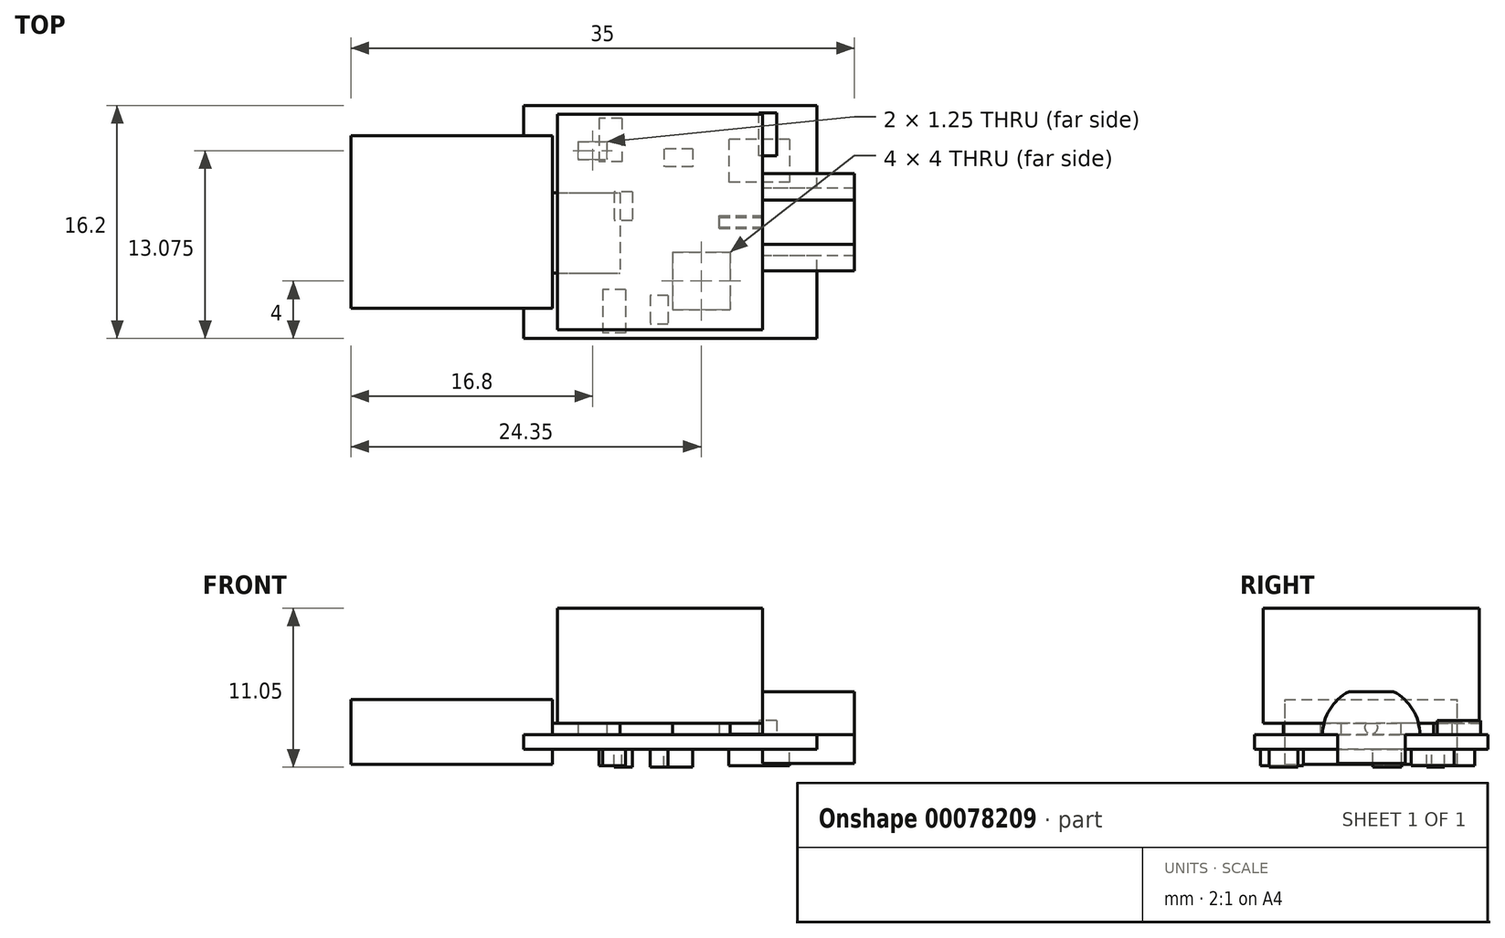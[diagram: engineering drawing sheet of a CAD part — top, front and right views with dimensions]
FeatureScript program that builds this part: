
annotation { "Feature Type Name" : "Feature", "Feature Type Description" : "" }
export const myFeature = defineFeature(function(context is Context, id is Id, definition is map)
    precondition{}
    {
        {
            var Q0;
            Q0=qCreatedBy(makeId("Top.planeOp"),FACE);
            var sketch = newSketch(context, id + "F0", { "sketchPlane" : qUnion([Q0])});
            skLineSegment(sketch, "E0.bottom", {"start": v(10.2, -8.1) * mm, "end": v(-10.2, -8.1) * mm});
            skLineSegment(sketch, "E0.top", {"start": v(10.2, 8.1) * mm, "end": v(-10.2, 8.1) * mm});
            skLineSegment(sketch, "E0.left", {"start": v(10.2, -8.1) * mm, "end": v(10.2, 8.1) * mm});
            skLineSegment(sketch, "E0.right", {"start": v(-10.2, -8.1) * mm, "end": v(-10.2, 8.1) * mm});
            skPoint(sketch, "E0.middle", {"position": v(0, 0) * mm});
            skSolve(sketch);
        }
        {
            var Q0;
            Q0=makeQuery(id+"F0.imprint","IMPRINT",FACE,{"disambiguationData":[TD([[makeQuery(id+"F0.imprint","IMPRINT",EDGE,{"derivedFrom":sQuery(id+"F0.wireOp",EDGE,"E0.bottom")}),-1.0]])]});
            extrude(context, id + "F1", {"entities" : qUnion([Q0]), "oppositeDirection" : true, "depth" : 1 * mm});
        }
        {
            var Q0;
            Q0=makeQuery(id+"F1.opExtrude","SWEPT_FACE",FACE,{"disambiguationData":[OSD([sQuery(id+"F0.wireOp",EDGE,"E0.right")])]});
            var sketch = newSketch(context, id + "F2", { "sketchPlane" : qUnion([Q0])});
            skLineSegment(sketch, "E1.bottom", {"start": v(6, -2.05) * mm, "end": v(-6, -2.05) * mm});
            skLineSegment(sketch, "E1.top", {"start": v(6, 2.45) * mm, "end": v(-6, 2.45) * mm});
            skLineSegment(sketch, "E1.left", {"start": v(6, -2.05) * mm, "end": v(6, 2.45) * mm});
            skLineSegment(sketch, "E1.right", {"start": v(-6, -2.05) * mm, "end": v(-6, 2.45) * mm});
            skPoint(sketch, "E1.middle", {"position": v(0, 0.2) * mm});
            skSolve(sketch);
        }
        {
            var Q0;
            Q0=qSketchRegion(id+"F2",true);
            extrude(context, id + "F3", {"entities" : qUnion([Q0]), "operationType" : NewBodyOperationType.ADD, "depth" : 12 * mm, "hasSecondDirection" : true, "secondDirectionOppositeDirection" : true, "secondDirectionDepth" : 2 * mm});
        }
        {
            var Q0;
            Q0=makeQuery(id+"F1.opExtrude","SWEPT_FACE",FACE,{"disambiguationData":[OSD([sQuery(id+"F0.wireOp",EDGE,"E0.left")])]});
            var sketch = newSketch(context, id + "F4", { "sketchPlane" : qUnion([Q0])});
            skLineSegment(sketch, "E2.top", {"start": v(-2.35, -2) * mm, "end": v(2.35, -2) * mm});
            skLineSegment(sketch, "E2.left", {"start": v(-2.35, 0) * mm, "end": v(-2.35, -2) * mm});
            skLineSegment(sketch, "E2.right", {"start": v(2.35, 0) * mm, "end": v(2.35, -2) * mm});
            skLineSegment(sketch, "E3", {"start": v(0, 0) * mm, "end": v(0, 1.3) * mm, "construction": true});
            skPoint(sketch, "E3.endSnap0", {"position": v(0, 0) * mm});
            skLineSegment(sketch, "E4", {"start": v(-2.35, 0) * mm, "end": v(-3.37, 0) * mm});
            skLineSegment(sketch, "E5", {"start": v(2.35, 0) * mm, "end": v(3.38, 0) * mm});
            skArc(sketch, "E6", {"start": v(3.38, 0) * mm, "mid": v(2.88, 1.76) * mm, "end": v(1.55, 3) * mm});
            skLineSegment(sketch, "E7", {"start": v(-1.55, 3) * mm, "end": v(1.55, 3) * mm});
            skArc(sketch, "E8.trimOffspring", {"start": v(-1.55, 3) * mm, "mid": v(-2.88, 1.76) * mm, "end": v(-3.37, 0) * mm});
            skSolve(sketch);
        }
        {
            var Q0;
            {var subQ0=sQuery(id+"F4.wireOp",EDGE,"E2.top");Q0=makeQuery(id+"F4.imprint","IMPRINT",FACE,{"disambiguationData":[TD([[makeQuery(id+"F4.imprint","IMPRINT",EDGE,{"derivedFrom":subQ0}),1.0]])]});}
            var Q1;
            {var subQ0=sQuery(id+"F4.wireOp",EDGE,"E2.left");var subQ1=sQuery(id+"F0.wireOp",EDGE,"E0.left");var subQ4=makeQuery(id+"F1.opExtrude","CAP_EDGE",EDGE,{"disambiguationData":[OSD([subQ1])],"isStart":false});var subQ5=makeQuery(id+"F4.imprint","INTERSECT",VERTEX,{"derivedFrom":[subQ4,subQ0]});Q1=makeQuery(id+"F4.imprint","IMPRINT",FACE,{"disambiguationData":[TD([[makeQuery(id+"F4.imprint","IMPRINT",EDGE,{"disambiguationData":[TD([[subQ5,-1.0]])],"derivedFrom":subQ4}),1.0]])]});}
            var Q2;
            {var subQ1=sQuery(id+"F4.wireOp",EDGE,"E4");Q2=makeQuery(id+"F4.imprint","IMPRINT",FACE,{"disambiguationData":[TD([[makeQuery(id+"F4.imprint","IMPRINT",EDGE,{"derivedFrom":subQ1}),1.0]])]});}
            extrude(context, id + "F5", {"entities" : qUnion([Q0, Q1, Q2]), "operationType" : NewBodyOperationType.ADD, "depth" : 2.6 * mm, "hasSecondDirection" : true, "secondDirectionOppositeDirection" : true, "secondDirectionDepth" : (6.4 - 2.6) * mm});
        }
        {
            var Q0;
            {var subQ0=sQuery(id+"F4.wireOp",EDGE,"E6");var subQ1=sQuery(id+"F4.wireOp",EDGE,"E7");var subQ2=sQuery(id+"F4.wireOp",EDGE,"E8.trimOffspring");Q0=makeQuery(id+"F5.boolean.opBoolean","SPLIT",FACE,{"disambiguationData":[TD([makeQuery(id+"F5.opExtrude","SWEPT_FACE",FACE,{"disambiguationData":[OSD([subQ0])]})])],"derivedFrom":makeQuery(id+"F5.opExtrude","CAP_FACE",FACE,{"disambiguationData":[OSD([sQuery(id+"F4.wireOp",EDGE,"E2.top"),sQuery(id+"F4.wireOp",EDGE,"E2.left"),sQuery(id+"F4.wireOp",EDGE,"E2.right"),sQuery(id+"F4.wireOp",EDGE,"E4"),sQuery(id+"F4.wireOp",EDGE,"E5"),subQ0,subQ1,subQ2])],"isStart":true})});}
            var sketch = newSketch(context, id + "F6", { "sketchPlane" : qUnion([Q0])});
            skCircle(sketch, "E9", {"center": v(0, 0.5) * mm, "radius": 0.45 * mm});
            skLineSegment(sketch, "E10.0.0", {"start": v(2.35, 0) * mm, "end": v(2.35, -2) * mm, "construction": true});
            skLineSegment(sketch, "E10.0.1", {"start": v(2.35, -2) * mm, "end": v(-2.35, -2) * mm, "construction": true});
            skLineSegment(sketch, "E10.0.2", {"start": v(-2.35, -2) * mm, "end": v(-2.35, 0) * mm, "construction": true});
            skLineSegment(sketch, "E10.0.3", {"start": v(-2.35, 0) * mm, "end": v(-3.38, 0) * mm, "construction": true});
            skArc(sketch, "E10.0.4", {"start": v(-3.38, 0) * mm, "mid": v(-2.88, 1.76) * mm, "end": v(-1.55, 3) * mm, "construction": true});
            skLineSegment(sketch, "E10.0.5", {"start": v(-1.55, 3) * mm, "end": v(1.55, 3) * mm, "construction": true});
            skArc(sketch, "E10.0.6", {"start": v(1.55, 3) * mm, "mid": v(2.88, 1.76) * mm, "end": v(3.37, 0) * mm, "construction": true});
            skLineSegment(sketch, "E10.0.7", {"start": v(3.37, 0) * mm, "end": v(2.35, 0) * mm, "construction": true});
            skCircle(sketch, "E11", {"center": v(0, 0.5) * mm, "radius": 1.73 * mm, "construction": true});
            skLineSegment(sketch, "E12", {"start": v(2.4, 0.5) * mm, "end": v(-2.45, 0.5) * mm, "construction": true});
            skSolve(sketch);
        }
        {
            var Q0;
            Q0=qSketchRegion(id+"F6",true);
            extrude(context, id + "F7", {"entities" : qUnion([Q0]), "operationType" : NewBodyOperationType.ADD, "depth" : 3 * mm});
        }
        {
            var Q0;
            Q0=makeQuery(id+"F1.opExtrude","CAP_FACE",FACE,{"disambiguationData":[OSD([sQuery(id+"F0.wireOp",EDGE,"E0.bottom"),sQuery(id+"F0.wireOp",EDGE,"E0.top"),sQuery(id+"F0.wireOp",EDGE,"E0.left"),sQuery(id+"F0.wireOp",EDGE,"E0.right")])],"isStart":true});
            var sketch = newSketch(context, id + "F8", { "sketchPlane" : qUnion([Q0])});
            skLineSegment(sketch, "E13.bottom", {"start": v(-9.1, 2.05) * mm, "end": v(-3.5, 2.05) * mm});
            skLineSegment(sketch, "E13.top", {"start": v(-9.1, -3.55) * mm, "end": v(-3.5, -3.55) * mm});
            skLineSegment(sketch, "E13.left", {"start": v(-9.1, 2.05) * mm, "end": v(-9.1, -3.55) * mm});
            skLineSegment(sketch, "E13.right", {"start": v(-3.5, 2.05) * mm, "end": v(-3.5, -3.55) * mm});
            skSolve(sketch);
        }
        {
            var Q0;
            Q0=qSketchRegion(id+"F8",true);
            extrude(context, id + "F9", {"entities" : qUnion([Q0]), "operationType" : NewBodyOperationType.ADD, "depth" : .8 * mm});
        }
        {
            var Q0;
            Q0=makeQuery(id+"F1.opExtrude","CAP_FACE",FACE,{"disambiguationData":[OSD([sQuery(id+"F0.wireOp",EDGE,"E0.bottom"),sQuery(id+"F0.wireOp",EDGE,"E0.top"),sQuery(id+"F0.wireOp",EDGE,"E0.left"),sQuery(id+"F0.wireOp",EDGE,"E0.right")])],"isStart":true});
            var sketch = newSketch(context, id + "F10", { "sketchPlane" : qUnion([Q0])});
            skLineSegment(sketch, "E14.bottom", {"start": v(0.15, -2.1) * mm, "end": v(4.15, -2.1) * mm});
            skLineSegment(sketch, "E14.top", {"start": v(0.15, -6.1) * mm, "end": v(4.15, -6.1) * mm});
            skLineSegment(sketch, "E14.left", {"start": v(0.15, -2.1) * mm, "end": v(0.15, -6.1) * mm});
            skLineSegment(sketch, "E14.right", {"start": v(4.15, -2.1) * mm, "end": v(4.15, -6.1) * mm});
            skSolve(sketch);
        }
        {
            var Q0;
            Q0=qSketchRegion(id+"F10",true);
            extrude(context, id + "F11", {"entities" : qUnion([Q0]), "operationType" : NewBodyOperationType.ADD, "depth" : .8 * mm});
        }
        {
            var Q0;
            Q0=makeQuery(id+"F1.opExtrude","CAP_FACE",FACE,{"disambiguationData":[OSD([sQuery(id+"F0.wireOp",EDGE,"E0.bottom"),sQuery(id+"F0.wireOp",EDGE,"E0.top"),sQuery(id+"F0.wireOp",EDGE,"E0.left"),sQuery(id+"F0.wireOp",EDGE,"E0.right")])],"isStart":true});
            var sketch = newSketch(context, id + "F12", { "sketchPlane" : qUnion([Q0])});
            skLineSegment(sketch, "E15.bottom", {"start": v(-6.4, 5.6) * mm, "end": v(-4.4, 5.6) * mm});
            skLineSegment(sketch, "E15.top", {"start": v(-6.4, 4.35) * mm, "end": v(-4.4, 4.35) * mm});
            skLineSegment(sketch, "E15.left", {"start": v(-6.4, 5.6) * mm, "end": v(-6.4, 4.35) * mm});
            skLineSegment(sketch, "E15.right", {"start": v(-4.4, 5.6) * mm, "end": v(-4.4, 4.35) * mm});
            skSolve(sketch);
        }
        {
            var Q0;
            Q0=qSketchRegion(id+"F12",true);
            extrude(context, id + "F13", {"entities" : qUnion([Q0]), "operationType" : NewBodyOperationType.ADD, "depth" : 1.25 * mm});
        }
        {
            var Q0;
            Q0=makeQuery(id+"F12.imprint","IMPRINT",FACE,{"disambiguationData":[TD([[makeQuery(id+"F12.imprint","IMPRINT",EDGE,{"derivedFrom":sQuery(id+"F12.wireOp",EDGE,"E15.bottom")}),1.0]])]});
            var sketch = newSketch(context, id + "F14", { "sketchPlane" : qUnion([Q0])});
            skLineSegment(sketch, "E16.bottom", {"start": v(7.4, 4.6) * mm, "end": v(6.15, 4.6) * mm});
            skLineSegment(sketch, "E16.top", {"start": v(7.4, 7.6) * mm, "end": v(6.15, 7.6) * mm});
            skLineSegment(sketch, "E16.left", {"start": v(7.4, 4.6) * mm, "end": v(7.4, 7.6) * mm});
            skLineSegment(sketch, "E16.right", {"start": v(6.15, 4.6) * mm, "end": v(6.15, 7.6) * mm});
            skSolve(sketch);
        }
        {
            var Q0;
            Q0=qSketchRegion(id+"F14",true);
            extrude(context, id + "F15", {"entities" : qUnion([Q0]), "operationType" : NewBodyOperationType.ADD, "depth" : 1 * mm});
        }
        {
            var Q0;
            Q0=makeQuery(id+"F1.opExtrude","CAP_FACE",FACE,{"disambiguationData":[OSD([sQuery(id+"F0.wireOp",EDGE,"E0.bottom"),sQuery(id+"F0.wireOp",EDGE,"E0.top"),sQuery(id+"F0.wireOp",EDGE,"E0.left"),sQuery(id+"F0.wireOp",EDGE,"E0.right")])],"isStart":false});
            var sketch = newSketch(context, id + "F16", { "sketchPlane" : qUnion([Q0])});
            skLineSegment(sketch, "E17.bottom", {"start": v(1.55, -5.1) * mm, "end": v(-0.45, -5.1) * mm});
            skLineSegment(sketch, "E17.top", {"start": v(1.55, -3.85) * mm, "end": v(-0.45, -3.85) * mm});
            skLineSegment(sketch, "E17.left", {"start": v(1.55, -5.1) * mm, "end": v(1.55, -3.85) * mm});
            skLineSegment(sketch, "E17.right", {"start": v(-0.45, -5.1) * mm, "end": v(-0.45, -3.85) * mm});
            skLineSegment(sketch, "E18.bottom", {"start": v(-2.65, -2.1) * mm, "end": v(-3.9, -2.1) * mm});
            skLineSegment(sketch, "E18.top", {"start": v(-2.65, -0.1) * mm, "end": v(-3.9, -0.1) * mm});
            skLineSegment(sketch, "E18.left", {"start": v(-2.65, -2.1) * mm, "end": v(-2.65, -0.1) * mm});
            skLineSegment(sketch, "E18.right", {"start": v(-3.9, -2.1) * mm, "end": v(-3.9, -0.1) * mm});
            skLineSegment(sketch, "E19.bottom", {"start": v(-0.15, 5.1) * mm, "end": v(-1.4, 5.1) * mm});
            skLineSegment(sketch, "E19.top", {"start": v(-0.15, 7.1) * mm, "end": v(-1.4, 7.1) * mm});
            skLineSegment(sketch, "E19.left", {"start": v(-0.15, 5.1) * mm, "end": v(-0.15, 7.1) * mm});
            skLineSegment(sketch, "E19.right", {"start": v(-1.4, 5.1) * mm, "end": v(-1.4, 7.1) * mm});
            skSolve(sketch);
        }
        {
            var Q0;
            Q0=qSketchRegion(id+"F16",true);
            extrude(context, id + "F17", {"entities" : qUnion([Q0]), "operationType" : NewBodyOperationType.ADD, "depth" : 1.25 * mm});
        }
        {
            var Q0;
            Q0=makeQuery(id+"F1.opExtrude","CAP_FACE",FACE,{"disambiguationData":[OSD([sQuery(id+"F0.wireOp",EDGE,"E0.bottom"),sQuery(id+"F0.wireOp",EDGE,"E0.top"),sQuery(id+"F0.wireOp",EDGE,"E0.left"),sQuery(id+"F0.wireOp",EDGE,"E0.right")])],"isStart":false});
            var sketch = newSketch(context, id + "F18", { "sketchPlane" : qUnion([Q0])});
            skLineSegment(sketch, "E20.bottom", {"start": v(-3.35, -7.2) * mm, "end": v(-4.95, -7.2) * mm});
            skLineSegment(sketch, "E20.top", {"start": v(-3.35, -4.2) * mm, "end": v(-4.95, -4.2) * mm});
            skLineSegment(sketch, "E20.left", {"start": v(-3.35, -7.2) * mm, "end": v(-3.35, -4.2) * mm});
            skLineSegment(sketch, "E20.right", {"start": v(-4.95, -7.2) * mm, "end": v(-4.95, -4.2) * mm});
            skLineSegment(sketch, "E21.bottom", {"start": v(-3.1, 4.7) * mm, "end": v(-4.7, 4.7) * mm});
            skLineSegment(sketch, "E21.top", {"start": v(-3.1, 7.7) * mm, "end": v(-4.7, 7.7) * mm});
            skLineSegment(sketch, "E21.left", {"start": v(-3.1, 4.7) * mm, "end": v(-3.1, 7.7) * mm});
            skLineSegment(sketch, "E21.right", {"start": v(-4.7, 4.7) * mm, "end": v(-4.7, 7.7) * mm});
            skSolve(sketch);
        }
        {
            var Q0;
            Q0=qSketchRegion(id+"F18",true);
            extrude(context, id + "F19", {"entities" : qUnion([Q0]), "operationType" : NewBodyOperationType.ADD, "depth" : 1.15 * mm});
        }
        {
            var Q0;
            Q0=makeQuery(id+"F1.opExtrude","CAP_FACE",FACE,{"disambiguationData":[OSD([sQuery(id+"F0.wireOp",EDGE,"E0.bottom"),sQuery(id+"F0.wireOp",EDGE,"E0.top"),sQuery(id+"F0.wireOp",EDGE,"E0.left"),sQuery(id+"F0.wireOp",EDGE,"E0.right")])],"isStart":false});
            var sketch = newSketch(context, id + "F20", { "sketchPlane" : qUnion([Q0])});
            skLineSegment(sketch, "E22.bottom", {"start": v(8.3, -5.77) * mm, "end": v(4.05, -5.77) * mm});
            skLineSegment(sketch, "E22.top", {"start": v(8.3, -2.77) * mm, "end": v(4.05, -2.77) * mm});
            skLineSegment(sketch, "E22.left", {"start": v(8.3, -5.77) * mm, "end": v(8.3, -2.77) * mm});
            skLineSegment(sketch, "E22.right", {"start": v(4.05, -5.77) * mm, "end": v(4.05, -2.77) * mm});
            skSolve(sketch);
        }
        {
            var Q0;
            Q0=qSketchRegion(id+"F20",true);
            extrude(context, id + "F21", {"entities" : qUnion([Q0]), "operationType" : NewBodyOperationType.ADD, "depth" : 1.15 * mm});
        }
        {
            var Q0;
            Q0=makeQuery(id+"F9.opExtrude","CAP_FACE",FACE,{"disambiguationData":[OSD([sQuery(id+"F8.wireOp",EDGE,"E13.bottom"),sQuery(id+"F8.wireOp",EDGE,"E13.top"),sQuery(id+"F8.wireOp",EDGE,"E13.left"),sQuery(id+"F8.wireOp",EDGE,"E13.right")])],"isStart":false});
            var sketch = newSketch(context, id + "F22", { "sketchPlane" : qUnion([Q0])});
            skLineSegment(sketch, "E23.bottom", {"start": v(-7.85, 7.5) * mm, "end": v(6.4, 7.5) * mm});
            skLineSegment(sketch, "E23.top", {"start": v(-7.85, -7.5) * mm, "end": v(6.4, -7.5) * mm});
            skLineSegment(sketch, "E23.left", {"start": v(-7.85, 7.5) * mm, "end": v(-7.85, -7.5) * mm});
            skLineSegment(sketch, "E23.right", {"start": v(6.4, 7.5) * mm, "end": v(6.4, -7.5) * mm});
            skLineSegment(sketch, "E24", {"start": v(12.8, 0) * mm, "end": v(-17.3, 0) * mm, "construction": true});
            skSolve(sketch);
        }
        {
            var Q0;
            Q0 = qSketchRegion(id + "F22", true);
            extrude(context, id + "F23", {"entities" : qUnion([Q0]), "operationType" : NewBodyOperationType.ADD, "depth" : 8 * mm, "offsetDistance" : 25 * mm});
        }
    });
